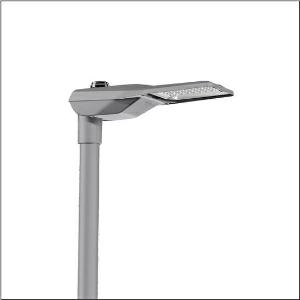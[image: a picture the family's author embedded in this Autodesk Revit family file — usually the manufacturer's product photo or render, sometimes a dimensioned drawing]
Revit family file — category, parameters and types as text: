
# Revit family: streetlight_sl_21_mini___pl52_5xe6h37n08gb_6e65
name_source: partatom
category: Lighting Fixtures
units: mm (PartAtom-declared; Revit-internal decimal feet)

## family parameters
Cut with Voids When Loaded = No
Host = Face
Light Source = No
Part Type = Normal
Room Calculation Point = No
Round Connector Dimension = Use Diameter
Shared = No

## types (1)
- --- (1 x LED, 5840 lm, 40.4 W, 3000K)
    Apparent Load = 40 VA
    CIE Flux Codes = 27 59 98 100 100
    Color Rendering = 70
    Color Temperature = 3000K
    Default Elevation = 1800 mm
    Description = Streetlight SL 21 mini, mast luminaire, primary light control with lens, of PMMA, primary optical cover: cover, of toughened safety glass, transparent, light distribution: PL52, light emission: direct distribution, primary light characteristic: asymmetric, installation type: side-entry, LED, 3G 1.5mm², High Power LED, rated luminous flux: 5.840lm, luminous efficacy: 145lm/W, light colour: 730, colour temperature: 3000K, control: overheat protection, pre-setting: linear dimming characteristic, constant luminous flux control, time-dependent luminous flux control, flexible luminous flux parameterisation, mains connection: 230..240V, AC, 50/60Hz, connection cable pre-assembled, cable length: 8,5m, wiring characteristics: H07RN-F, start of lifetime: 40W, end of service life: 41W, reduction: 19W, luminaire housing, of diecast aluminium (EN AC-44300), powder-coated, Siteco® metallic grey (DB 702S), corrosivity category C5 mid according to DIN EN ISO 12944, multi-level sealing system, sealing non-destructively replaceable, inclination adjustable: 0°, 5°, 10°, 15°, length: 628mm, width: 235mm, height: 110mm, spigot size: 42mm (side-entry), protection rating (complete): IP66, insulation class (complete): insulation class I (protective earthing), certification: CE, ENEC, ENEC+, VDE, impact resistance: IK09, permissible operating ambient temperature for outdoor applications: -40..+50°C, standard-compliant lighting for roads and squares, packaging unit: 1 piece

Light Distribution: PL52
    Height = 110 mm
    Lamp = 1 x LED
    Lamp Light Flux = 5840 lm
    Lamp Power = 40.4 W
    Lamp count = 1
    Length = 625 mm
    Luminous efficacy = 145 lm/W
    Manufacturer = Siteco
    ModVariant = No
    Model = 5XE6H37N08GB
    Number of Poles = 1
    OnlyDefault = Yes
    Power Factor = 1
    Product Name = Streetlight SL 21 mini | PL52
    Product group = mast luminaire | pylon top
    ProductGroupID = 6100
    Protection Class = Protection class I
    Protection Degree = IP 66
    RLX_Detail_Level = 1
    RLX_Emergency_Light_Flux = 0 lm
    RLX_Emergency_Type = 0
    RLX_Emergency_Type_DB = No
    RlxData = <blob elided: 101349 chars, md5=652bfee7>
    Socket = socket
    Standby Power = 0 W
    System Light Flux = 5840 lm
    System Power = 40 W
    Type Comments = factory setting: luminous flux: 100 % | dim-lin: 254 | 812 mA
    Type Image = l_1294379.jpg
    URL = http://relux.com
    VarID = @adj_106887
    Voltage = 0 V
    Weight = 0.00 kg
    Width = 234 mm

## geometry (parser evidence)
native form markers: Blend x4, Sweep x9
no freeform markers — native parametric forms only
